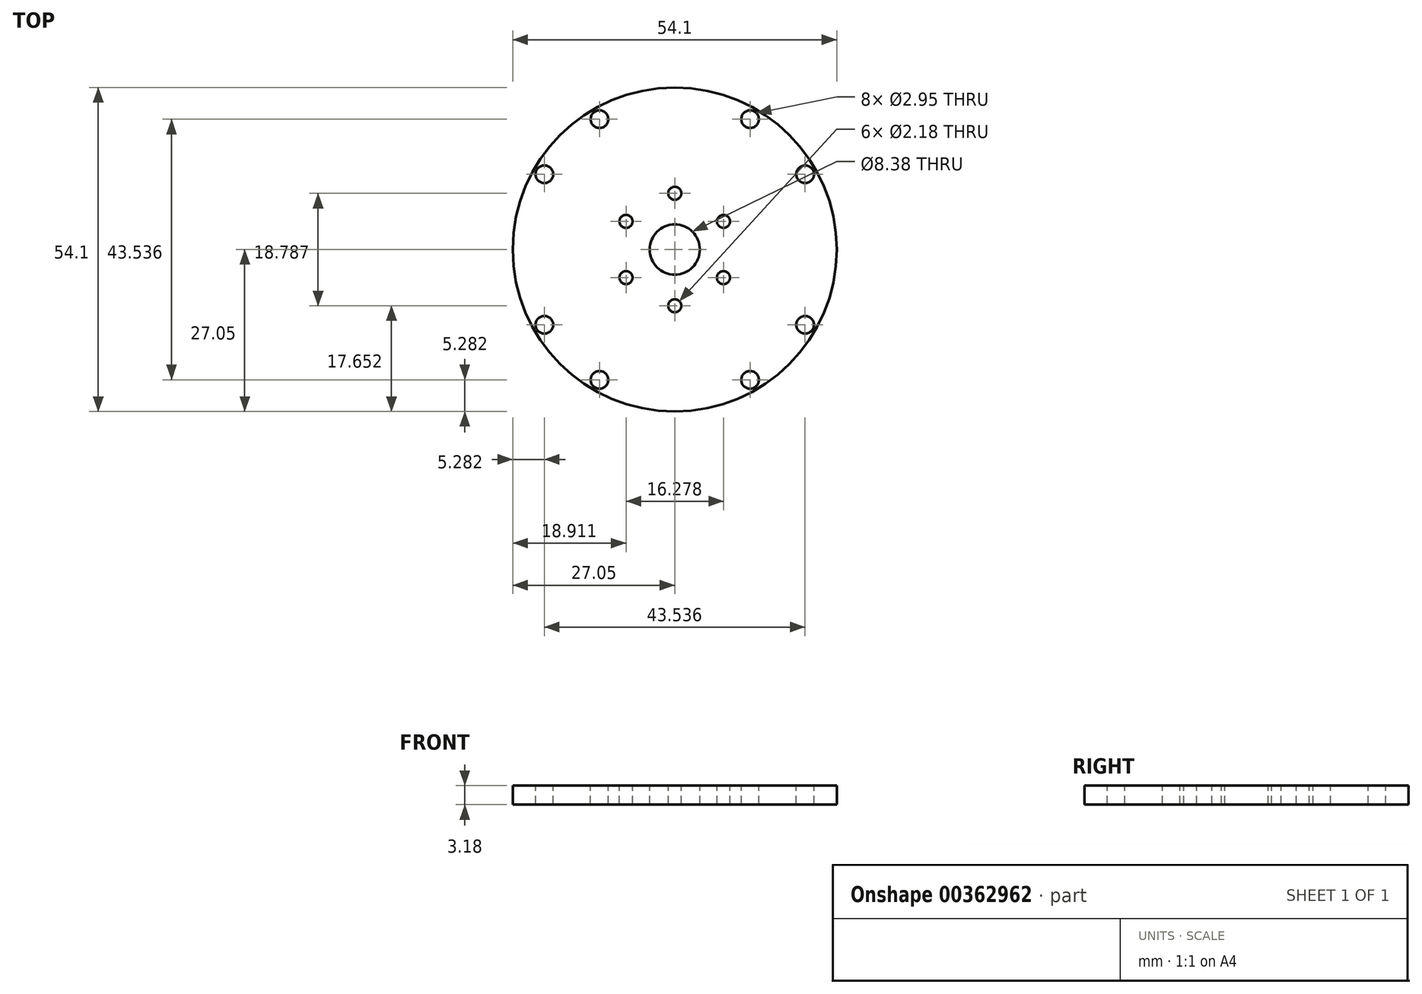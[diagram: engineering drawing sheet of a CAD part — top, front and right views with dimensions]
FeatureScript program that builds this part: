
annotation { "Feature Type Name" : "Feature", "Feature Type Description" : "" }
export const myFeature = defineFeature(function(context is Context, id is Id, definition is map)
    precondition{}
    {
        {
            var Q0;
            Q0=qCreatedBy(makeId("Top.planeOp"),FACE);
            var sketch = newSketch(context, id + "F0", { "sketchPlane" : qUnion([Q0])});
            skCircle(sketch, "E0", {"center": v(0, 0) * mm, "radius": 27.05 * mm});
            skSolve(sketch);
        }
        {
            var Q0;
            Q0=makeQuery(id+"F0.imprint","IMPRINT",FACE,{"disambiguationData":[TD([[makeQuery(id+"F0.imprint","IMPRINT",EDGE,{"derivedFrom":sQuery(id+"F0.wireOp",EDGE,"E0")}),1.0]])]});
            extrude(context, id + "F1", {"entities" : qUnion([Q0]), "depth" : 3.17 * mm});
        }
        {
            var Q0;
            Q0=makeQuery(id+"F1.opExtrude","CAP_FACE",FACE,{"disambiguationData":[OSD([sQuery(id+"F0.wireOp",EDGE,"E0")])],"isStart":false});
            var sketch = newSketch(context, id + "F2", { "sketchPlane" : qUnion([Q0])});
            skPoint(sketch, "E1", {"position": v(0, 0) * mm});
            skPoint(sketch, "E2", {"position": v(12.57, 21.77) * mm});
            skPoint(sketch, "E3", {"position": v(21.77, 12.57) * mm});
            skPoint(sketch, "E4.1.0", {"position": v(-21.77, 12.57) * mm});
            skPoint(sketch, "E4.1.1", {"position": v(-12.57, 21.77) * mm});
            skPoint(sketch, "E4.2.0", {"position": v(-12.57, -21.77) * mm});
            skPoint(sketch, "E4.2.1", {"position": v(-21.77, -12.57) * mm});
            skPoint(sketch, "E4.3.0", {"position": v(21.77, -12.57) * mm});
            skPoint(sketch, "E4.3.1", {"position": v(12.57, -21.77) * mm});
            skSolve(sketch);
        }
        {
            var Q0;
            Q0=makeQuery(id+"F2.imprint","IMPRINT",FACE,{"disambiguationData":[TD([[makeQuery(id+"F2.imprint","IMPRINT",EDGE,{"derivedFrom":makeQuery(id+"F1.opExtrude","CAP_EDGE",EDGE,{"disambiguationData":[OSD([sQuery(id+"F0.wireOp",EDGE,"E0")])],"isStart":false})}),1.0]])]});
            var sketch = newSketch(context, id + "F3", { "sketchPlane" : qUnion([Q0])});
            skPoint(sketch, "E5", {"position": v(8.13, -4.7) * mm});
            skPoint(sketch, "E6", {"position": v(0, -9.4) * mm});
            skPoint(sketch, "E7.1.0", {"position": v(0, 9.39) * mm});
            skPoint(sketch, "E7.1.1", {"position": v(8.14, 4.7) * mm});
            skPoint(sketch, "E7.2.0", {"position": v(-8.13, -4.69) * mm});
            skPoint(sketch, "E7.2.1", {"position": v(-8.14, 4.7) * mm});
            skPoint(sketch, "E7.center", {"position": v(0, 0) * mm});
            skSolve(sketch);
        }
        {
            var Q0;
            Q0=sQuery(id+"F2.wireOp",VERTEX,"E2");
            var Q1;
            Q1=sQuery(id+"F2.wireOp",VERTEX,"E3");
            var Q2;
            Q2=sQuery(id+"F2.wireOp",VERTEX,"E4.3.0");
            var Q3;
            Q3=sQuery(id+"F2.wireOp",VERTEX,"E4.3.1");
            var Q4;
            Q4=sQuery(id+"F2.wireOp",VERTEX,"E4.2.0");
            var Q5;
            Q5=sQuery(id+"F2.wireOp",VERTEX,"E4.1.1");
            var Q6;
            Q6=sQuery(id+"F2.wireOp",VERTEX,"E4.1.0");
            var Q7;
            Q7=sQuery(id+"F2.wireOp",VERTEX,"E4.2.1");
            var Q8;
            Q8=makeQuery(id+"F1.opExtrude","SWEPT_BODY",BODY,{"disambiguationData":[OSD([sQuery(id+"F0.wireOp",EDGE,"E0")])]});
            hole(context, id + "F4", {"style" : HoleStyle.SIMPLE, "endStyle" : HoleEndStyle.THROUGH, "standardTappedOrClearance" : lookupTablePath({ "standard" : "ANSI", "size" : "#32 (0.12)", "type" : "Drilled" }), "standardBlindInLast" : lookupTablePath({ "standard" : "ANSI", "size" : "#32", "type" : "Drilled" }), "holeDiameter" : 2.95 * mm, "isTappedThrough" : true, "tappedDepth" : 6.35 * mm, "tapClearance" : 3, "startFromSketch" : true, "locations" : qUnion([Q0, Q1, Q2, Q3, Q4, Q5, Q6, Q7]), "scope" : qUnion([Q8])});
        }
        {
            var Q0;
            Q0=sQuery(id+"F3.wireOp",VERTEX,"E5");
            var Q1;
            Q1=sQuery(id+"F3.wireOp",VERTEX,"E7.1.1");
            var Q2;
            Q2=sQuery(id+"F3.wireOp",VERTEX,"E7.1.0");
            var Q3;
            Q3=sQuery(id+"F3.wireOp",VERTEX,"E7.2.1");
            var Q4;
            Q4=sQuery(id+"F3.wireOp",VERTEX,"E7.2.0");
            var Q5;
            Q5=sQuery(id+"F3.wireOp",VERTEX,"E6");
            var Q6;
            Q6=makeQuery(id+"F1.opExtrude","SWEPT_BODY",BODY,{"disambiguationData":[OSD([sQuery(id+"F0.wireOp",EDGE,"E0")])]});
            hole(context, id + "F5", {"style" : HoleStyle.SIMPLE, "endStyle" : HoleEndStyle.THROUGH, "standardTappedOrClearance" : lookupTablePath({ "standard" : "ANSI", "size" : "#44 (0.09)", "type" : "Drilled" }), "standardBlindInLast" : lookupTablePath({ "standard" : "ANSI", "size" : "#44", "type" : "Drilled" }), "holeDiameter" : 2.18 * mm, "isTappedThrough" : true, "tappedDepth" : 6.35 * mm, "tapClearance" : 3, "startFromSketch" : true, "locations" : qUnion([Q0, Q1, Q2, Q3, Q4, Q5]), "scope" : qUnion([Q6])});
        }
        {
            var Q0;
            Q0=makeQuery(id+"F1.opExtrude","CAP_FACE",FACE,{"disambiguationData":[OSD([sQuery(id+"F0.wireOp",EDGE,"E0")])],"isStart":false});
            var sketch = newSketch(context, id + "F6", { "sketchPlane" : qUnion([Q0])});
            skPoint(sketch, "E8", {"position": v(0, 0) * mm});
            skSolve(sketch);
        }
        {
            var Q0;
            Q0=sQuery(id+"F6.wireOp",VERTEX,"E8");
            var Q1;
            Q1=makeQuery(id+"F1.opExtrude","SWEPT_BODY",BODY,{"disambiguationData":[OSD([sQuery(id+"F0.wireOp",EDGE,"E0")])]});
            hole(context, id + "F7", {"style" : HoleStyle.SIMPLE, "endStyle" : HoleEndStyle.THROUGH, "holeDiameter" : 8.38 * mm, "isTappedThrough" : true, "tappedDepth" : 6.35 * mm, "tapClearance" : 3, "startFromSketch" : true, "locations" : qUnion([Q0]), "scope" : qUnion([Q1])});
        }
    });
